# Revit family: Casement_34_I_Top_Hung_Standard
name_source: partatom
category: Windows
revit_build: Autodesk Revit 2014 (Build: 20130308_1515(x64)
units: mm (PartAtom-declared; Revit-internal decimal feet)

## types (21) — shared parameters
Aluminium Thickness = 1 mm  [stored 0.00328084 ft]
Bead SG Gap = 13 mm  [stored 0.0426509 ft]
Bottom Hung = No
Casement Dimension = 34 mm
Custom Sash Bottom Height = 554 mm  [stored 1.81759 ft]
Custom Sash Top Height = 554 mm  [stored 1.81759 ft]
DG Extrusion Start = 7 mm  [stored 0.0229659 ft]
DG Gasket Finish = Double Glazing Gasket Material
Default Sill Height = 800 mm  [stored 2.62467 ft]
Depth Bead = 20 mm  [stored 0.0656168 ft]
Description = Window 34mm, Type I top hung
Frame Center Offset = 17 mm
Height Panel 1 = 540 mm  [stored 1.77165 ft]
Height Panel 2 = 540 mm  [stored 1.77165 ft]
Height Sash Bottom = 524 mm  [stored 1.71916 ft]
Height Sash Bottom Opening = 554 mm  [stored 1.81759 ft]
Height Sash Top = 524 mm  [stored 1.71916 ft]
Height Sash Top Opening = 554 mm  [stored 1.81759 ft]
Limit Fixed Pane Height Max = 1800 mm
Limit Fixed Pane Height Min = 200 mm  [stored 0.656168 ft]
Limit Fixed Pane Width Max = 1500 mm
Limit Fixed Pane Width Min = 200 mm  [stored 0.656168 ft]
Limit Sash Bottom Height Min = 300 mm  [stored 0.984252 ft]
Limit Sash Top Height Max = 900 mm  [stored 2.95276 ft]
Limit Sash Top Height Min = 300 mm  [stored 0.984252 ft]
Limit Sash Width Max = 1200 mm
Limit Sash Width Min = 300 mm  [stored 0.984252 ft]
Limit Window Height Max = 1860 mm
Limit Window Height Min = 1400 mm
Manufacturer = Crealco
Max System DG One Piece Thickness = 4 mm  [stored 0.0131234 ft]
Max System DG Unit Thickness = 20 mm  [stored 0.0656168 ft]
Model = Casement 34
Offset Bead SG Center Reversed = 17 mm
Offset Panel 3 Bead Top = 1170 mm
Offset Sash 1 Top = 23 mm  [stored 0.0754593 ft]
Offset Sash 2 Top = 593 mm  [stored 1.94554 ft]
Offset Sash Left = 23 mm  [stored 0.0754593 ft]
Offset Transom 1 Top = 570 mm  [stored 1.87008 ft]
Offset Transom 2 Top = 1140 mm
Offset Window Exterior = 17 mm
SG Gasket Thickness = 6 mm  [stored 0.019685 ft]
Sash Center Offset = 14 mm  [stored 0.0459318 ft]
Sash Overlap = 7 mm  [stored 0.0229659 ft]
Sash Spacing Inner = 8 mm  [stored 0.0262467 ft]
Top Hung = Yes
URL = http://www.crealco.co.za
Wall Closure = By host
Width Bead = 15 mm  [stored 0.0492126 ft]
Width Profile = 30 mm  [stored 0.0984252 ft]
zero-valued in all types: Window Exterior Offset

## per-type parameters (varying)
- 34-1215DT-1000Pa: Area Pane Left Bottom=0.15 m²; Area Pane Left Middle=0.23 m²; Area Pane Left Top=0.23 m²; Area Pane Right=0.78 m²; Clearvue Insulated LowE SHGC Value=0.717; Clearvue Insulated LowE U Value=5.06; Clearvue Insulated SHGC Value=0.801; Clearvue Insulated U Value=5.68; Clearvue SHGC Value=0.885; Custom Sash Width=554 mm  [stored 1.81759 ft]; Custom Windload=1000 mm; Custom Window Height=1490 mm; Custom Window Width=1190 mm; DG Thickness Calc=4 mm  [stored 0.0131234 ft]; Depth Mullion=54 mm  [stored 0.177165 ft]; Energy Advantage SHGC Value=0.793; Energy Advantage U Value=6.76; Height=1490 mm; Height Panel 3=290 mm  [stored 0.951444 ft]; Height Panel 4=1430 mm; Intruderprufe LowE SHGC Value=0.744; Intruderprufe LowE U Value=6.53; Intruderprufe SHGC Value=0.834; Length Mullion=1490 mm; Length Transom=540 mm  [stored 1.77165 ft]; Limit Sash Bottom Height Max=644 mm  [stored 2.11286 ft]; Limit Sash Bottom Height Max Based On Top Sash=644 mm  [stored 2.11286 ft]; Limit Sash Bottom Height Max Calc=644 mm  [stored 2.11286 ft]; Limit Window Width Max=2130 mm; Limit Window Width Min=830 mm  [stored 2.7231 ft]; Max Pane Area=0.78 m²; Mullion Depth Windload Based=54 mm  [stored 0.177165 ft]; Offset Mullion Left=570 mm  [stored 1.87008 ft]; Offset Panel 4 Left=600 mm  [stored 1.9685 ft]; Width=1190 mm; Width Panel 1=540 mm  [stored 1.77165 ft]; Width Panel 2=540 mm  [stored 1.77165 ft]; Width Panel 3=540 mm  [stored 1.77165 ft]; Width Panel 4=560 mm  [stored 1.83727 ft]; Width Sash 1=524 mm  [stored 1.71916 ft]; Width Sash 2=524 mm  [stored 1.71916 ft]; Width Sash Opening=554 mm  [stored 1.81759 ft]; Windload Design=1000 mm
- 34-1215DT-1500Pa: Area Pane Left Bottom=0.15 m²; Area Pane Left Middle=0.23 m²; Area Pane Left Top=0.23 m²; Area Pane Right=0.78 m²; Clearvue Insulated LowE SHGC Value=0.717; Clearvue Insulated LowE U Value=5.06; Clearvue Insulated SHGC Value=0.801; Clearvue Insulated U Value=5.68; Clearvue SHGC Value=0.885; Custom Sash Width=554 mm  [stored 1.81759 ft]; Custom Windload=1500 mm; Custom Window Height=1490 mm; Custom Window Width=1190 mm; DG Thickness Calc=4 mm  [stored 0.0131234 ft]; Depth Mullion=54 mm  [stored 0.177165 ft]; Energy Advantage SHGC Value=0.793; Energy Advantage U Value=6.76; Height=1490 mm; Height Panel 3=290 mm  [stored 0.951444 ft]; Height Panel 4=1430 mm; Intruderprufe LowE SHGC Value=0.744; Intruderprufe LowE U Value=6.53; Intruderprufe SHGC Value=0.834; Length Mullion=1490 mm; Length Transom=540 mm  [stored 1.77165 ft]; Limit Sash Bottom Height Max=644 mm  [stored 2.11286 ft]; Limit Sash Bottom Height Max Based On Top Sash=644 mm  [stored 2.11286 ft]; Limit Sash Bottom Height Max Calc=644 mm  [stored 2.11286 ft]; Limit Window Width Max=2130 mm; Limit Window Width Min=830 mm  [stored 2.7231 ft]; Max Pane Area=0.78 m²; Mullion Depth Windload Based=54 mm  [stored 0.177165 ft]; Offset Mullion Left=570 mm  [stored 1.87008 ft]; Offset Panel 4 Left=600 mm  [stored 1.9685 ft]; Width=1190 mm; Width Panel 1=540 mm  [stored 1.77165 ft]; Width Panel 2=540 mm  [stored 1.77165 ft]; Width Panel 3=540 mm  [stored 1.77165 ft]; Width Panel 4=560 mm  [stored 1.83727 ft]; Width Sash 1=524 mm  [stored 1.71916 ft]; Width Sash 2=524 mm  [stored 1.71916 ft]; Width Sash Opening=554 mm  [stored 1.81759 ft]; Windload Design=1500 mm
- 34-1215DT-2000Pa: Area Pane Left Bottom=0.15 m²; Area Pane Left Middle=0.23 m²; Area Pane Left Top=0.23 m²; Area Pane Right=0.78 m²; Clearvue Insulated LowE SHGC Value=0.717; Clearvue Insulated LowE U Value=5.06; Clearvue Insulated SHGC Value=0.801; Clearvue Insulated U Value=5.68; Clearvue SHGC Value=0.885; Custom Sash Width=554 mm  [stored 1.81759 ft]; Custom Windload=2000 mm; Custom Window Height=1490 mm; Custom Window Width=1190 mm; DG Thickness Calc=4 mm  [stored 0.0131234 ft]; Depth Mullion=54 mm  [stored 0.177165 ft]; Energy Advantage SHGC Value=0.793; Energy Advantage U Value=6.76; Height=1490 mm; Height Panel 3=290 mm  [stored 0.951444 ft]; Height Panel 4=1430 mm; Intruderprufe LowE SHGC Value=0.744; Intruderprufe LowE U Value=6.53; Intruderprufe SHGC Value=0.834; Length Mullion=1490 mm; Length Transom=540 mm  [stored 1.77165 ft]; Limit Sash Bottom Height Max=644 mm  [stored 2.11286 ft]; Limit Sash Bottom Height Max Based On Top Sash=644 mm  [stored 2.11286 ft]; Limit Sash Bottom Height Max Calc=644 mm  [stored 2.11286 ft]; Limit Window Width Max=2130 mm; Limit Window Width Min=830 mm  [stored 2.7231 ft]; Max Pane Area=0.78 m²; Mullion Depth Windload Based=54 mm  [stored 0.177165 ft]; Offset Mullion Left=570 mm  [stored 1.87008 ft]; Offset Panel 4 Left=600 mm  [stored 1.9685 ft]; Width=1190 mm; Width Panel 1=540 mm  [stored 1.77165 ft]; Width Panel 2=540 mm  [stored 1.77165 ft]; Width Panel 3=540 mm  [stored 1.77165 ft]; Width Panel 4=560 mm  [stored 1.83727 ft]; Width Sash 1=524 mm  [stored 1.71916 ft]; Width Sash 2=524 mm  [stored 1.71916 ft]; Width Sash Opening=554 mm  [stored 1.81759 ft]; Windload Design=2000 mm
- 34-1515DT-1000Pa: Area Pane Left Bottom=0.15 m²; Area Pane Left Middle=0.23 m²; Area Pane Left Top=0.23 m²; Area Pane Right=1.21 m²; Clearvue Insulated LowE SHGC Value=0.829; Clearvue Insulated LowE U Value=5.14; Clearvue Insulated SHGC Value=0.923; Clearvue Insulated U Value=5.92; Clearvue SHGC Value=1.026; Custom Sash Width=554 mm  [stored 1.81759 ft]; Custom Windload=1000 mm; Custom Window Height=1490 mm; Custom Window Width=1490 mm; DG Thickness Calc=4 mm  [stored 0.0131234 ft]; Depth Mullion=54 mm  [stored 0.177165 ft]; Energy Advantage SHGC Value=0.919; Energy Advantage U Value=7.15; Height=1490 mm; Height Panel 3=290 mm  [stored 0.951444 ft]; Height Panel 4=1430 mm; Intruderprufe LowE SHGC Value=0.86; Intruderprufe LowE U Value=6.89; Intruderprufe SHGC Value=0.968; Length Mullion=1490 mm; Length Transom=540 mm  [stored 1.77165 ft]; Limit Sash Bottom Height Max=644 mm  [stored 2.11286 ft]; Limit Sash Bottom Height Max Based On Top Sash=644 mm  [stored 2.11286 ft]; Limit Sash Bottom Height Max Calc=644 mm  [stored 2.11286 ft]; Limit Window Width Max=2130 mm; Limit Window Width Min=830 mm  [stored 2.7231 ft]; Max Pane Area=1.21 m²; Mullion Depth Windload Based=54 mm  [stored 0.177165 ft]; Offset Mullion Left=570 mm  [stored 1.87008 ft]; Offset Panel 4 Left=600 mm  [stored 1.9685 ft]; Width=1490 mm; Width Panel 1=540 mm  [stored 1.77165 ft]; Width Panel 2=540 mm  [stored 1.77165 ft]; Width Panel 3=540 mm  [stored 1.77165 ft]; Width Panel 4=860 mm  [stored 2.82152 ft]; Width Sash 1=524 mm  [stored 1.71916 ft]; Width Sash 2=524 mm  [stored 1.71916 ft]; Width Sash Opening=554 mm  [stored 1.81759 ft]; Windload Design=1000 mm
- 34-1515DT-1500Pa: Area Pane Left Bottom=0.15 m²; Area Pane Left Middle=0.23 m²; Area Pane Left Top=0.23 m²; Area Pane Right=1.21 m²; Clearvue Insulated LowE SHGC Value=0.829; Clearvue Insulated LowE U Value=5.14; Clearvue Insulated SHGC Value=0.923; Clearvue Insulated U Value=5.92; Clearvue SHGC Value=1.026; Custom Sash Width=554 mm  [stored 1.81759 ft]; Custom Windload=1500 mm; Custom Window Height=1490 mm; Custom Window Width=1490 mm; DG Thickness Calc=4 mm  [stored 0.0131234 ft]; Depth Mullion=54 mm  [stored 0.177165 ft]; Energy Advantage SHGC Value=0.919; Energy Advantage U Value=7.15; Height=1490 mm; Height Panel 3=290 mm  [stored 0.951444 ft]; Height Panel 4=1430 mm; Intruderprufe LowE SHGC Value=0.86; Intruderprufe LowE U Value=6.89; Intruderprufe SHGC Value=0.968; Length Mullion=1490 mm; Length Transom=540 mm  [stored 1.77165 ft]; Limit Sash Bottom Height Max=644 mm  [stored 2.11286 ft]; Limit Sash Bottom Height Max Based On Top Sash=644 mm  [stored 2.11286 ft]; Limit Sash Bottom Height Max Calc=644 mm  [stored 2.11286 ft]; Limit Window Width Max=2130 mm; Limit Window Width Min=830 mm  [stored 2.7231 ft]; Max Pane Area=1.21 m²; Mullion Depth Windload Based=54 mm  [stored 0.177165 ft]; Offset Mullion Left=570 mm  [stored 1.87008 ft]; Offset Panel 4 Left=600 mm  [stored 1.9685 ft]; Width=1490 mm; Width Panel 1=540 mm  [stored 1.77165 ft]; Width Panel 2=540 mm  [stored 1.77165 ft]; Width Panel 3=540 mm  [stored 1.77165 ft]; Width Panel 4=860 mm  [stored 2.82152 ft]; Width Sash 1=524 mm  [stored 1.71916 ft]; Width Sash 2=524 mm  [stored 1.71916 ft]; Width Sash Opening=554 mm  [stored 1.81759 ft]; Windload Design=1500 mm
- 34-1515DT-2000Pa: Area Pane Left Bottom=0.15 m²; Area Pane Left Middle=0.23 m²; Area Pane Left Top=0.23 m²; Area Pane Right=1.21 m²; Clearvue Insulated LowE SHGC Value=0.831; Clearvue Insulated LowE U Value=5.18; Clearvue Insulated SHGC Value=0.913; Clearvue Insulated U Value=6.05; Clearvue SHGC Value=1.027; Custom Sash Width=554 mm  [stored 1.81759 ft]; Custom Windload=2000 mm; Custom Window Height=1490 mm; Custom Window Width=1490 mm; DG Thickness Calc=4 mm  [stored 0.0131234 ft]; Depth Mullion=70 mm  [stored 0.229659 ft]; Energy Advantage SHGC Value=0.919; Energy Advantage U Value=7.23; Height=1490 mm; Height Panel 3=290 mm  [stored 0.951444 ft]; Height Panel 4=1430 mm; Intruderprufe LowE SHGC Value=0.861; Intruderprufe LowE U Value=6.96; Intruderprufe SHGC Value=0.97; Length Mullion=1490 mm; Length Transom=540 mm  [stored 1.77165 ft]; Limit Sash Bottom Height Max=644 mm  [stored 2.11286 ft]; Limit Sash Bottom Height Max Based On Top Sash=644 mm  [stored 2.11286 ft]; Limit Sash Bottom Height Max Calc=644 mm  [stored 2.11286 ft]; Limit Window Width Max=2130 mm; Limit Window Width Min=830 mm  [stored 2.7231 ft]; Max Pane Area=1.21 m²; Mullion Depth Windload Based=70 mm  [stored 0.229659 ft]; Offset Mullion Left=570 mm  [stored 1.87008 ft]; Offset Panel 4 Left=600 mm  [stored 1.9685 ft]; Width=1490 mm; Width Panel 1=540 mm  [stored 1.77165 ft]; Width Panel 2=540 mm  [stored 1.77165 ft]; Width Panel 3=540 mm  [stored 1.77165 ft]; Width Panel 4=860 mm  [stored 2.82152 ft]; Width Sash 1=524 mm  [stored 1.71916 ft]; Width Sash 2=524 mm  [stored 1.71916 ft]; Width Sash Opening=554 mm  [stored 1.81759 ft]; Windload Design=2000 mm
- 34-1218DT-1000Pa: Area Pane Left Bottom=0.31 m²; Area Pane Left Middle=0.23 m²; Area Pane Left Top=0.23 m²; Area Pane Right=0.95 m²; Clearvue Insulated LowE SHGC Value=0.774; Clearvue Insulated LowE U Value=5.14; Clearvue Insulated SHGC Value=0.864; Clearvue Insulated U Value=5.83; Clearvue SHGC Value=0.956; Custom Sash Width=554 mm  [stored 1.81759 ft]; Custom Windload=1000 mm; Custom Window Height=1790 mm; Custom Window Width=1190 mm; DG Thickness Calc=4 mm  [stored 0.0131234 ft]; Depth Mullion=54 mm  [stored 0.177165 ft]; Energy Advantage SHGC Value=0.857; Energy Advantage U Value=6.99; Height=1790 mm; Height Panel 3=590 mm; Height Panel 4=1730 mm; Intruderprufe LowE SHGC Value=0.803; Intruderprufe LowE U Value=6.77; Intruderprufe SHGC Value=0.902; Length Mullion=1790 mm; Length Transom=540 mm  [stored 1.77165 ft]; Limit Sash Bottom Height Max=900 mm  [stored 2.95276 ft]; Limit Sash Bottom Height Max Based On Top Sash=944 mm; Limit Sash Bottom Height Max Calc=900 mm  [stored 2.95276 ft]; Limit Window Width Max=2130 mm; Limit Window Width Min=830 mm  [stored 2.7231 ft]; Max Pane Area=0.95 m²; Mullion Depth Windload Based=54 mm  [stored 0.177165 ft]; Offset Mullion Left=570 mm  [stored 1.87008 ft]; Offset Panel 4 Left=600 mm  [stored 1.9685 ft]; Width=1190 mm; Width Panel 1=540 mm  [stored 1.77165 ft]; Width Panel 2=540 mm  [stored 1.77165 ft]; Width Panel 3=540 mm  [stored 1.77165 ft]; Width Panel 4=560 mm  [stored 1.83727 ft]; Width Sash 1=524 mm  [stored 1.71916 ft]; Width Sash 2=524 mm  [stored 1.71916 ft]; Width Sash Opening=554 mm  [stored 1.81759 ft]; Windload Design=1000 mm
- 34-1218DT-1500Pa: Area Pane Left Bottom=0.31 m²; Area Pane Left Middle=0.23 m²; Area Pane Left Top=0.23 m²; Area Pane Right=0.95 m²; Clearvue Insulated LowE SHGC Value=0.776; Clearvue Insulated LowE U Value=5.19; Clearvue Insulated SHGC Value=0.852; Clearvue Insulated U Value=5.98; Clearvue SHGC Value=0.957; Custom Sash Width=554 mm  [stored 1.81759 ft]; Custom Windload=1500 mm; Custom Window Height=1790 mm; Custom Window Width=1190 mm; DG Thickness Calc=4 mm  [stored 0.0131234 ft]; Depth Mullion=70 mm  [stored 0.229659 ft]; Energy Advantage SHGC Value=0.857; Energy Advantage U Value=7.08; Height=1790 mm; Height Panel 3=590 mm; Height Panel 4=1730 mm; Intruderprufe LowE SHGC Value=0.803; Intruderprufe LowE U Value=6.84; Intruderprufe SHGC Value=0.903; Length Mullion=1790 mm; Length Transom=540 mm  [stored 1.77165 ft]; Limit Sash Bottom Height Max=900 mm  [stored 2.95276 ft]; Limit Sash Bottom Height Max Based On Top Sash=944 mm; Limit Sash Bottom Height Max Calc=900 mm  [stored 2.95276 ft]; Limit Window Width Max=2130 mm; Limit Window Width Min=830 mm  [stored 2.7231 ft]; Max Pane Area=0.95 m²; Mullion Depth Windload Based=70 mm  [stored 0.229659 ft]; Offset Mullion Left=570 mm  [stored 1.87008 ft]; Offset Panel 4 Left=600 mm  [stored 1.9685 ft]; Width=1190 mm; Width Panel 1=540 mm  [stored 1.77165 ft]; Width Panel 2=540 mm  [stored 1.77165 ft]; Width Panel 3=540 mm  [stored 1.77165 ft]; Width Panel 4=560 mm  [stored 1.83727 ft]; Width Sash 1=524 mm  [stored 1.71916 ft]; Width Sash 2=524 mm  [stored 1.71916 ft]; Width Sash Opening=554 mm  [stored 1.81759 ft]; Windload Design=1500 mm
- 34-1218DT-2000Pa: Area Pane Left Bottom=0.31 m²; Area Pane Left Middle=0.23 m²; Area Pane Left Top=0.23 m²; Area Pane Right=0.95 m²; Clearvue Insulated LowE SHGC Value=0.776; Clearvue Insulated LowE U Value=5.19; Clearvue Insulated SHGC Value=0.852; Clearvue Insulated U Value=5.98; Clearvue SHGC Value=0.957; Custom Sash Width=554 mm  [stored 1.81759 ft]; Custom Windload=2000 mm; Custom Window Height=1790 mm; Custom Window Width=1190 mm; DG Thickness Calc=4 mm  [stored 0.0131234 ft]; Depth Mullion=70 mm  [stored 0.229659 ft]; Energy Advantage SHGC Value=0.857; Energy Advantage U Value=7.08; Height=1790 mm; Height Panel 3=590 mm; Height Panel 4=1730 mm; Intruderprufe LowE SHGC Value=0.803; Intruderprufe LowE U Value=6.84; Intruderprufe SHGC Value=0.903; Length Mullion=1790 mm; Length Transom=540 mm  [stored 1.77165 ft]; Limit Sash Bottom Height Max=900 mm  [stored 2.95276 ft]; Limit Sash Bottom Height Max Based On Top Sash=944 mm; Limit Sash Bottom Height Max Calc=900 mm  [stored 2.95276 ft]; Limit Window Width Max=2130 mm; Limit Window Width Min=830 mm  [stored 2.7231 ft]; Max Pane Area=0.95 m²; Mullion Depth Windload Based=70 mm  [stored 0.229659 ft]; Offset Mullion Left=570 mm  [stored 1.87008 ft]; Offset Panel 4 Left=600 mm  [stored 1.9685 ft]; Width=1190 mm; Width Panel 1=540 mm  [stored 1.77165 ft]; Width Panel 2=540 mm  [stored 1.77165 ft]; Width Panel 3=540 mm  [stored 1.77165 ft]; Width Panel 4=560 mm  [stored 1.83727 ft]; Width Sash 1=524 mm  [stored 1.71916 ft]; Width Sash 2=524 mm  [stored 1.71916 ft]; Width Sash Opening=554 mm  [stored 1.81759 ft]; Windload Design=2000 mm
- 34-1518DT-1000Pa: Area Pane Left Bottom=0.31 m²; Area Pane Left Middle=0.23 m²; Area Pane Left Top=0.23 m²; Area Pane Right=1.46 m²; Clearvue Insulated LowE SHGC Value=0.908; Clearvue Insulated LowE U Value=5.35; Clearvue Insulated SHGC Value=0.998; Clearvue Insulated U Value=6.31; Clearvue SHGC Value=0; Custom Sash Width=554 mm  [stored 1.81759 ft]; Custom Windload=1000 mm; Custom Window Height=1790 mm; Custom Window Width=1490 mm; DG Thickness Calc=4 mm  [stored 0.0131234 ft]; Depth Mullion=70 mm  [stored 0.229659 ft]; Energy Advantage SHGC Value=0; Energy Advantage U Value=7.9; Height=1790 mm; Height Panel 3=590 mm; Height Panel 4=1730 mm; Intruderprufe LowE SHGC Value=0.94; Intruderprufe LowE U Value=7.33; Intruderprufe SHGC Value=1.061; Length Mullion=1790 mm; Length Transom=540 mm  [stored 1.77165 ft]; Limit Sash Bottom Height Max=900 mm  [stored 2.95276 ft]; Limit Sash Bottom Height Max Based On Top Sash=944 mm; Limit Sash Bottom Height Max Calc=900 mm  [stored 2.95276 ft]; Limit Window Width Max=2130 mm; Limit Window Width Min=830 mm  [stored 2.7231 ft]; Max Pane Area=1.46 m²; Mullion Depth Windload Based=70 mm  [stored 0.229659 ft]; Offset Mullion Left=570 mm  [stored 1.87008 ft]; Offset Panel 4 Left=600 mm  [stored 1.9685 ft]; Width=1490 mm; Width Panel 1=540 mm  [stored 1.77165 ft]; Width Panel 2=540 mm  [stored 1.77165 ft]; Width Panel 3=540 mm  [stored 1.77165 ft]; Width Panel 4=860 mm  [stored 2.82152 ft]; Width Sash 1=524 mm  [stored 1.71916 ft]; Width Sash 2=524 mm  [stored 1.71916 ft]; Width Sash Opening=554 mm  [stored 1.81759 ft]; Windload Design=1000 mm
- 34-1518DT-1500Pa: Area Pane Left Bottom=0.31 m²; Area Pane Left Middle=0.23 m²; Area Pane Left Top=0.23 m²; Area Pane Right=1.46 m²; Clearvue Insulated LowE SHGC Value=0.908; Clearvue Insulated LowE U Value=5.35; Clearvue Insulated SHGC Value=0.998; Clearvue Insulated U Value=6.31; Clearvue SHGC Value=0; Custom Sash Width=554 mm  [stored 1.81759 ft]; Custom Windload=1500 mm; Custom Window Height=1790 mm; Custom Window Width=1490 mm; DG Thickness Calc=4 mm  [stored 0.0131234 ft]; Depth Mullion=70 mm  [stored 0.229659 ft]; Energy Advantage SHGC Value=0; Energy Advantage U Value=7.9; Height=1790 mm; Height Panel 3=590 mm; Height Panel 4=1730 mm; Intruderprufe LowE SHGC Value=0.94; Intruderprufe LowE U Value=7.33; Intruderprufe SHGC Value=1.061; Length Mullion=1790 mm; Length Transom=540 mm  [stored 1.77165 ft]; Limit Sash Bottom Height Max=900 mm  [stored 2.95276 ft]; Limit Sash Bottom Height Max Based On Top Sash=944 mm; Limit Sash Bottom Height Max Calc=900 mm  [stored 2.95276 ft]; Limit Window Width Max=2130 mm; Limit Window Width Min=830 mm  [stored 2.7231 ft]; Max Pane Area=1.46 m²; Mullion Depth Windload Based=70 mm  [stored 0.229659 ft]; Offset Mullion Left=570 mm  [stored 1.87008 ft]; Offset Panel 4 Left=600 mm  [stored 1.9685 ft]; Width=1490 mm; Width Panel 1=540 mm  [stored 1.77165 ft]; Width Panel 2=540 mm  [stored 1.77165 ft]; Width Panel 3=540 mm  [stored 1.77165 ft]; Width Panel 4=860 mm  [stored 2.82152 ft]; Width Sash 1=524 mm  [stored 1.71916 ft]; Width Sash 2=524 mm  [stored 1.71916 ft]; Width Sash Opening=554 mm  [stored 1.81759 ft]; Windload Design=1500 mm
- 34-1815DT-1000Pa: Area Pane Left Bottom=0.25 m²; Area Pane Left Middle=0.4 m²; Area Pane Left Top=0.4 m²; Area Pane Right=1.14 m²; Clearvue Insulated LowE SHGC Value=0.761; Clearvue Insulated LowE U Value=4.64; Clearvue Insulated SHGC Value=0.846; Clearvue Insulated U Value=5.38; Clearvue SHGC Value=0.943; Custom Sash Width=900 mm  [stored 2.95276 ft]; Custom Windload=1000 mm; Custom Window Height=1490 mm; Custom Window Width=1790 mm; DG Thickness Calc=4 mm  [stored 0.0131234 ft]; Depth Mullion=54 mm  [stored 0.177165 ft]; Energy Advantage SHGC Value=0.844; Energy Advantage U Value=6.46; Height=1490 mm; Height Panel 3=290 mm  [stored 0.951444 ft]; Height Panel 4=1430 mm; Intruderprufe LowE SHGC Value=0.79; Intruderprufe LowE U Value=6.27; Intruderprufe SHGC Value=0.89; Length Mullion=1490 mm; Length Transom=886 mm  [stored 2.90682 ft]; Limit Sash Bottom Height Max=644 mm  [stored 2.11286 ft]; Limit Sash Bottom Height Max Based On Top Sash=644 mm  [stored 2.11286 ft]; Limit Sash Bottom Height Max Calc=644 mm  [stored 2.11286 ft]; Limit Window Width Max=2476 mm; Limit Window Width Min=1176 mm; Max Pane Area=1.14 m²; Mullion Depth Windload Based=54 mm  [stored 0.177165 ft]; Offset Mullion Left=916 mm  [stored 3.00525 ft]; Offset Panel 4 Left=946 mm; Width=1790 mm; Width Panel 1=886 mm  [stored 2.90682 ft]; Width Panel 2=886 mm  [stored 2.90682 ft]; Width Panel 3=886 mm  [stored 2.90682 ft]; Width Panel 4=814 mm; Width Sash 1=870 mm  [stored 2.85433 ft]; Width Sash 2=870 mm  [stored 2.85433 ft]; Width Sash Opening=900 mm  [stored 2.95276 ft]; Windload Design=1000 mm
- 34-1815DT-1500Pa: Area Pane Left Bottom=0.25 m²; Area Pane Left Middle=0.4 m²; Area Pane Left Top=0.4 m²; Area Pane Right=1.14 m²; Clearvue Insulated LowE SHGC Value=0.763; Clearvue Insulated LowE U Value=4.67; Clearvue Insulated SHGC Value=0.838; Clearvue Insulated U Value=5.48; Clearvue SHGC Value=0.943; Custom Sash Width=900 mm  [stored 2.95276 ft]; Custom Windload=1500 mm; Custom Window Height=1490 mm; Custom Window Width=1790 mm; DG Thickness Calc=4 mm  [stored 0.0131234 ft]; Depth Mullion=70 mm  [stored 0.229659 ft]; Energy Advantage SHGC Value=0.844; Energy Advantage U Value=6.55; Height=1490 mm; Height Panel 3=290 mm  [stored 0.951444 ft]; Height Panel 4=1430 mm; Intruderprufe LowE SHGC Value=0.79; Intruderprufe LowE U Value=6.32; Intruderprufe SHGC Value=0.891; Length Mullion=1490 mm; Length Transom=886 mm  [stored 2.90682 ft]; Limit Sash Bottom Height Max=644 mm  [stored 2.11286 ft]; Limit Sash Bottom Height Max Based On Top Sash=644 mm  [stored 2.11286 ft]; Limit Sash Bottom Height Max Calc=644 mm  [stored 2.11286 ft]; Limit Window Width Max=2476 mm; Limit Window Width Min=1176 mm; Max Pane Area=1.14 m²; Mullion Depth Windload Based=70 mm  [stored 0.229659 ft]; Offset Mullion Left=916 mm  [stored 3.00525 ft]; Offset Panel 4 Left=946 mm; Width=1790 mm; Width Panel 1=886 mm  [stored 2.90682 ft]; Width Panel 2=886 mm  [stored 2.90682 ft]; Width Panel 3=886 mm  [stored 2.90682 ft]; Width Panel 4=814 mm; Width Sash 1=870 mm  [stored 2.85433 ft]; Width Sash 2=870 mm  [stored 2.85433 ft]; Width Sash Opening=900 mm  [stored 2.95276 ft]; Windload Design=1500 mm
- 34-1815DT-2000Pa: Area Pane Left Bottom=0.25 m²; Area Pane Left Middle=0.4 m²; Area Pane Left Top=0.4 m²; Area Pane Right=0.72 m²; Clearvue Insulated LowE SHGC Value=0.763; Clearvue Insulated LowE U Value=4.67; Clearvue Insulated SHGC Value=0.838; Clearvue Insulated U Value=5.48; Clearvue SHGC Value=0.943; Custom Sash Width=900 mm  [stored 2.95276 ft]; Custom Windload=2000 mm; Custom Window Height=1490 mm; Custom Window Width=1490 mm; DG Thickness Calc=4 mm  [stored 0.0131234 ft]; Depth Mullion=70 mm  [stored 0.229659 ft]; Energy Advantage SHGC Value=0.844; Energy Advantage U Value=6.55; Height=1490 mm; Height Panel 3=290 mm  [stored 0.951444 ft]; Height Panel 4=1430 mm; Intruderprufe LowE SHGC Value=0.79; Intruderprufe LowE U Value=6.32; Intruderprufe SHGC Value=0.891; Length Mullion=1490 mm; Length Transom=886 mm  [stored 2.90682 ft]; Limit Sash Bottom Height Max=644 mm  [stored 2.11286 ft]; Limit Sash Bottom Height Max Based On Top Sash=644 mm  [stored 2.11286 ft]; Limit Sash Bottom Height Max Calc=644 mm  [stored 2.11286 ft]; Limit Window Width Max=2476 mm; Limit Window Width Min=1176 mm; Max Pane Area=0.72 m²; Mullion Depth Windload Based=70 mm  [stored 0.229659 ft]; Offset Mullion Left=916 mm  [stored 3.00525 ft]; Offset Panel 4 Left=946 mm; Width=1490 mm; Width Panel 1=886 mm  [stored 2.90682 ft]; Width Panel 2=886 mm  [stored 2.90682 ft]; Width Panel 3=886 mm  [stored 2.90682 ft]; Width Panel 4=514 mm; Width Sash 1=870 mm  [stored 2.85433 ft]; Width Sash 2=870 mm  [stored 2.85433 ft]; Width Sash Opening=900 mm  [stored 2.95276 ft]; Windload Design=2000 mm
- 34-2415DT-1000Pa: Area Pane Left Bottom=0.25 m²; Area Pane Left Middle=0.4 m²; Area Pane Left Top=0.4 m²; Area Pane Right=1.99 m²; Clearvue Insulated LowE SHGC Value=0.898; Clearvue Insulated LowE U Value=4.81; Clearvue Insulated SHGC Value=0.995; Clearvue Insulated U Value=5.73; Clearvue SHGC Value=0; Custom Sash Width=900 mm  [stored 2.95276 ft]; Custom Windload=1000 mm; Custom Window Height=1490 mm; Custom Window Width=2390 mm; DG Thickness Calc=4 mm  [stored 0.0131234 ft]; Depth Mullion=54 mm  [stored 0.177165 ft]; Energy Advantage SHGC Value=0; Energy Advantage U Value=7.9; Height=1490 mm; Height Panel 3=290 mm  [stored 0.951444 ft]; Height Panel 4=1430 mm; Intruderprufe LowE SHGC Value=0.931; Intruderprufe LowE U Value=6.77; Intruderprufe SHGC Value=1.053; Length Mullion=1490 mm; Length Transom=886 mm  [stored 2.90682 ft]; Limit Sash Bottom Height Max=644 mm  [stored 2.11286 ft]; Limit Sash Bottom Height Max Based On Top Sash=644 mm  [stored 2.11286 ft]; Limit Sash Bottom Height Max Calc=644 mm  [stored 2.11286 ft]; Limit Window Width Max=2476 mm; Limit Window Width Min=1176 mm; Max Pane Area=1.99 m²; Mullion Depth Windload Based=54 mm  [stored 0.177165 ft]; Offset Mullion Left=916 mm  [stored 3.00525 ft]; Offset Panel 4 Left=946 mm; Width=2390 mm; Width Panel 1=886 mm  [stored 2.90682 ft]; Width Panel 2=886 mm  [stored 2.90682 ft]; Width Panel 3=886 mm  [stored 2.90682 ft]; Width Panel 4=1414 mm; Width Sash 1=870 mm  [stored 2.85433 ft]; Width Sash 2=870 mm  [stored 2.85433 ft]; Width Sash Opening=900 mm  [stored 2.95276 ft]; Windload Design=1000 mm
- 34-2415DT-1500Pa: Area Pane Left Bottom=0.25 m²; Area Pane Left Middle=0.4 m²; Area Pane Left Top=0.4 m²; Area Pane Right=1.99 m²; Clearvue Insulated LowE SHGC Value=0.899; Clearvue Insulated LowE U Value=4.84; Clearvue Insulated SHGC Value=0.988; Clearvue Insulated U Value=5.81; Clearvue SHGC Value=0; Custom Sash Width=900 mm  [stored 2.95276 ft]; Custom Windload=1500 mm; Custom Window Height=1490 mm; Custom Window Width=2390 mm; DG Thickness Calc=4 mm  [stored 0.0131234 ft]; Depth Mullion=70 mm  [stored 0.229659 ft]; Energy Advantage SHGC Value=0; Energy Advantage U Value=7.9; Height=1490 mm; Height Panel 3=290 mm  [stored 0.951444 ft]; Height Panel 4=1430 mm; Intruderprufe LowE SHGC Value=0.931; Intruderprufe LowE U Value=6.81; Intruderprufe SHGC Value=1.053; Length Mullion=1490 mm; Length Transom=886 mm  [stored 2.90682 ft]; Limit Sash Bottom Height Max=644 mm  [stored 2.11286 ft]; Limit Sash Bottom Height Max Based On Top Sash=644 mm  [stored 2.11286 ft]; Limit Sash Bottom Height Max Calc=644 mm  [stored 2.11286 ft]; Limit Window Width Max=2476 mm; Limit Window Width Min=1176 mm; Max Pane Area=1.99 m²; Mullion Depth Windload Based=70 mm  [stored 0.229659 ft]; Offset Mullion Left=916 mm  [stored 3.00525 ft]; Offset Panel 4 Left=946 mm; Width=2390 mm; Width Panel 1=886 mm  [stored 2.90682 ft]; Width Panel 2=886 mm  [stored 2.90682 ft]; Width Panel 3=886 mm  [stored 2.90682 ft]; Width Panel 4=1414 mm; Width Sash 1=870 mm  [stored 2.85433 ft]; Width Sash 2=870 mm  [stored 2.85433 ft]; Width Sash Opening=900 mm  [stored 2.95276 ft]; Windload Design=1500 mm
- 34-2415DT-2000Pa: Area Pane Left Bottom=0.25 m²; Area Pane Left Middle=0.4 m²; Area Pane Left Top=0.4 m²; Area Pane Right=1.99 m²; Clearvue Insulated LowE SHGC Value=0.899; Clearvue Insulated LowE U Value=4.84; Clearvue Insulated SHGC Value=0.988; Clearvue Insulated U Value=5.81; Clearvue SHGC Value=0; Custom Sash Width=900 mm  [stored 2.95276 ft]; Custom Windload=2000 mm; Custom Window Height=1490 mm; Custom Window Width=2390 mm; DG Thickness Calc=4 mm  [stored 0.0131234 ft]; Depth Mullion=70 mm  [stored 0.229659 ft]; Energy Advantage SHGC Value=0; Energy Advantage U Value=7.9; Height=1490 mm; Height Panel 3=290 mm  [stored 0.951444 ft]; Height Panel 4=1430 mm; Intruderprufe LowE SHGC Value=0.931; Intruderprufe LowE U Value=6.81; Intruderprufe SHGC Value=1.053; Length Mullion=1490 mm; Length Transom=886 mm  [stored 2.90682 ft]; Limit Sash Bottom Height Max=644 mm  [stored 2.11286 ft]; Limit Sash Bottom Height Max Based On Top Sash=644 mm  [stored 2.11286 ft]; Limit Sash Bottom Height Max Calc=644 mm  [stored 2.11286 ft]; Limit Window Width Max=2476 mm; Limit Window Width Min=1176 mm; Max Pane Area=1.99 m²; Mullion Depth Windload Based=70 mm  [stored 0.229659 ft]; Offset Mullion Left=916 mm  [stored 3.00525 ft]; Offset Panel 4 Left=946 mm; Width=2390 mm; Width Panel 1=886 mm  [stored 2.90682 ft]; Width Panel 2=886 mm  [stored 2.90682 ft]; Width Panel 3=886 mm  [stored 2.90682 ft]; Width Panel 4=1414 mm; Width Sash 1=870 mm  [stored 2.85433 ft]; Width Sash 2=870 mm  [stored 2.85433 ft]; Width Sash Opening=900 mm  [stored 2.95276 ft]; Windload Design=2000 mm
- 34-1818DT-1000Pa: Area Pane Left Bottom=0.51 m²; Area Pane Left Middle=0.4 m²; Area Pane Left Top=0.4 m²; Area Pane Right=1.38 m²; Clearvue Insulated LowE SHGC Value=0.822; Clearvue Insulated LowE U Value=4.73; Clearvue Insulated SHGC Value=0.904; Clearvue Insulated U Value=5.6; Clearvue SHGC Value=0; Custom Sash Width=900 mm  [stored 2.95276 ft]; Custom Windload=1000 mm; Custom Window Height=1790 mm; Custom Window Width=1790 mm; DG Thickness Calc=4 mm  [stored 0.0131234 ft]; Depth Mullion=70 mm  [stored 0.229659 ft]; Energy Advantage SHGC Value=0; Energy Advantage U Value=7.9; Height=1790 mm; Height Panel 3=590 mm; Height Panel 4=1730 mm; Intruderprufe LowE SHGC Value=0.852; Intruderprufe LowE U Value=6.54; Intruderprufe SHGC Value=0.962; Length Mullion=1790 mm; Length Transom=886 mm  [stored 2.90682 ft]; Limit Sash Bottom Height Max=900 mm  [stored 2.95276 ft]; Limit Sash Bottom Height Max Based On Top Sash=944 mm; Limit Sash Bottom Height Max Calc=900 mm  [stored 2.95276 ft]; Limit Window Width Max=2476 mm; Limit Window Width Min=1176 mm; Max Pane Area=1.38 m²; Mullion Depth Windload Based=70 mm  [stored 0.229659 ft]; Offset Mullion Left=916 mm  [stored 3.00525 ft]; Offset Panel 4 Left=946 mm; Width=1790 mm; Width Panel 1=886 mm  [stored 2.90682 ft]; Width Panel 2=886 mm  [stored 2.90682 ft]; Width Panel 3=886 mm  [stored 2.90682 ft]; Width Panel 4=814 mm; Width Sash 1=870 mm  [stored 2.85433 ft]; Width Sash 2=870 mm  [stored 2.85433 ft]; Width Sash Opening=900 mm  [stored 2.95276 ft]; Windload Design=1000 mm
- 34-1818DT-1500Pa: Area Pane Left Bottom=0.51 m²; Area Pane Left Middle=0.4 m²; Area Pane Left Top=0.4 m²; Area Pane Right=1.38 m²; Clearvue Insulated LowE SHGC Value=0.822; Clearvue Insulated LowE U Value=4.73; Clearvue Insulated SHGC Value=0.904; Clearvue Insulated U Value=5.6; Clearvue SHGC Value=0; Custom Sash Width=900 mm  [stored 2.95276 ft]; Custom Windload=1500 mm; Custom Window Height=1790 mm; Custom Window Width=1790 mm; DG Thickness Calc=4 mm  [stored 0.0131234 ft]; Depth Mullion=70 mm  [stored 0.229659 ft]; Energy Advantage SHGC Value=0; Energy Advantage U Value=7.9; Height=1790 mm; Height Panel 3=590 mm; Height Panel 4=1730 mm; Intruderprufe LowE SHGC Value=0.852; Intruderprufe LowE U Value=6.54; Intruderprufe SHGC Value=0.962; Length Mullion=1790 mm; Length Transom=886 mm  [stored 2.90682 ft]; Limit Sash Bottom Height Max=900 mm  [stored 2.95276 ft]; Limit Sash Bottom Height Max Based On Top Sash=944 mm; Limit Sash Bottom Height Max Calc=900 mm  [stored 2.95276 ft]; Limit Window Width Max=2476 mm; Limit Window Width Min=1176 mm; Max Pane Area=1.38 m²; Mullion Depth Windload Based=70 mm  [stored 0.229659 ft]; Offset Mullion Left=916 mm  [stored 3.00525 ft]; Offset Panel 4 Left=946 mm; Width=1790 mm; Width Panel 1=886 mm  [stored 2.90682 ft]; Width Panel 2=886 mm  [stored 2.90682 ft]; Width Panel 3=886 mm  [stored 2.90682 ft]; Width Panel 4=814 mm; Width Sash 1=870 mm  [stored 2.85433 ft]; Width Sash 2=870 mm  [stored 2.85433 ft]; Width Sash Opening=900 mm  [stored 2.95276 ft]; Windload Design=1500 mm
- 34-2418DT-1000Pa: Area Pane Left Bottom=0.51 m²; Area Pane Left Middle=0.4 m²; Area Pane Left Top=0.4 m²; Area Pane Right=2.41 m²; Clearvue Insulated LowE SHGC Value=0; Clearvue Insulated LowE U Value=7.9; Clearvue Insulated SHGC Value=0; Clearvue Insulated U Value=7.9; Clearvue SHGC Value=0; Custom Sash Width=900 mm  [stored 2.95276 ft]; Custom Windload=1000 mm; Custom Window Height=1790 mm; Custom Window Width=2390 mm; DG Thickness Calc=5 mm  [stored 0.0164042 ft]; Depth Mullion=70 mm  [stored 0.229659 ft]; Energy Advantage SHGC Value=0; Energy Advantage U Value=7.9; Height=1790 mm; Height Panel 3=590 mm; Height Panel 4=1730 mm; Intruderprufe LowE SHGC Value=1.02; Intruderprufe LowE U Value=7.21; Intruderprufe SHGC Value=1.155; Length Mullion=1790 mm; Length Transom=886 mm  [stored 2.90682 ft]; Limit Sash Bottom Height Max=900 mm  [stored 2.95276 ft]; Limit Sash Bottom Height Max Based On Top Sash=944 mm; Limit Sash Bottom Height Max Calc=900 mm  [stored 2.95276 ft]; Limit Window Width Max=2476 mm; Limit Window Width Min=1176 mm; Max Pane Area=2.41 m²; Mullion Depth Windload Based=70 mm  [stored 0.229659 ft]; Offset Mullion Left=916 mm  [stored 3.00525 ft]; Offset Panel 4 Left=946 mm; Width=2390 mm; Width Panel 1=886 mm  [stored 2.90682 ft]; Width Panel 2=886 mm  [stored 2.90682 ft]; Width Panel 3=886 mm  [stored 2.90682 ft]; Width Panel 4=1414 mm; Width Sash 1=870 mm  [stored 2.85433 ft]; Width Sash 2=870 mm  [stored 2.85433 ft]; Width Sash Opening=900 mm  [stored 2.95276 ft]; Windload Design=1000 mm
- 34-2418DT-1500Pa: Area Pane Left Bottom=0.51 m²; Area Pane Left Middle=0.4 m²; Area Pane Left Top=0.4 m²; Area Pane Right=2.41 m²; Clearvue Insulated LowE SHGC Value=0; Clearvue Insulated LowE U Value=7.9; Clearvue Insulated SHGC Value=0; Clearvue Insulated U Value=7.9; Clearvue SHGC Value=0; Custom Sash Width=900 mm  [stored 2.95276 ft]; Custom Windload=1500 mm; Custom Window Height=1790 mm; Custom Window Width=2390 mm; DG Thickness Calc=5 mm  [stored 0.0164042 ft]; Depth Mullion=70 mm  [stored 0.229659 ft]; Energy Advantage SHGC Value=0; Energy Advantage U Value=7.9; Height=1790 mm; Height Panel 3=590 mm; Height Panel 4=1730 mm; Intruderprufe LowE SHGC Value=1.02; Intruderprufe LowE U Value=7.21; Intruderprufe SHGC Value=1.155; Length Mullion=1790 mm; Length Transom=886 mm  [stored 2.90682 ft]; Limit Sash Bottom Height Max=900 mm  [stored 2.95276 ft]; Limit Sash Bottom Height Max Based On Top Sash=944 mm; Limit Sash Bottom Height Max Calc=900 mm  [stored 2.95276 ft]; Limit Window Width Max=2476 mm; Limit Window Width Min=1176 mm; Max Pane Area=2.41 m²; Mullion Depth Windload Based=70 mm  [stored 0.229659 ft]; Offset Mullion Left=916 mm  [stored 3.00525 ft]; Offset Panel 4 Left=946 mm; Width=2390 mm; Width Panel 1=886 mm  [stored 2.90682 ft]; Width Panel 2=886 mm  [stored 2.90682 ft]; Width Panel 3=886 mm  [stored 2.90682 ft]; Width Panel 4=1414 mm; Width Sash 1=870 mm  [stored 2.85433 ft]; Width Sash 2=870 mm  [stored 2.85433 ft]; Width Sash Opening=900 mm  [stored 2.95276 ft]; Windload Design=1500 mm

note: [stored X ft] marks values corroborated as IEEE doubles in the binary element streams (Revit-internal decimal feet)

## geometry (parser evidence)
native form markers: Blend x4, Extrusion x1, Sweep x28
no freeform markers — native parametric forms only
